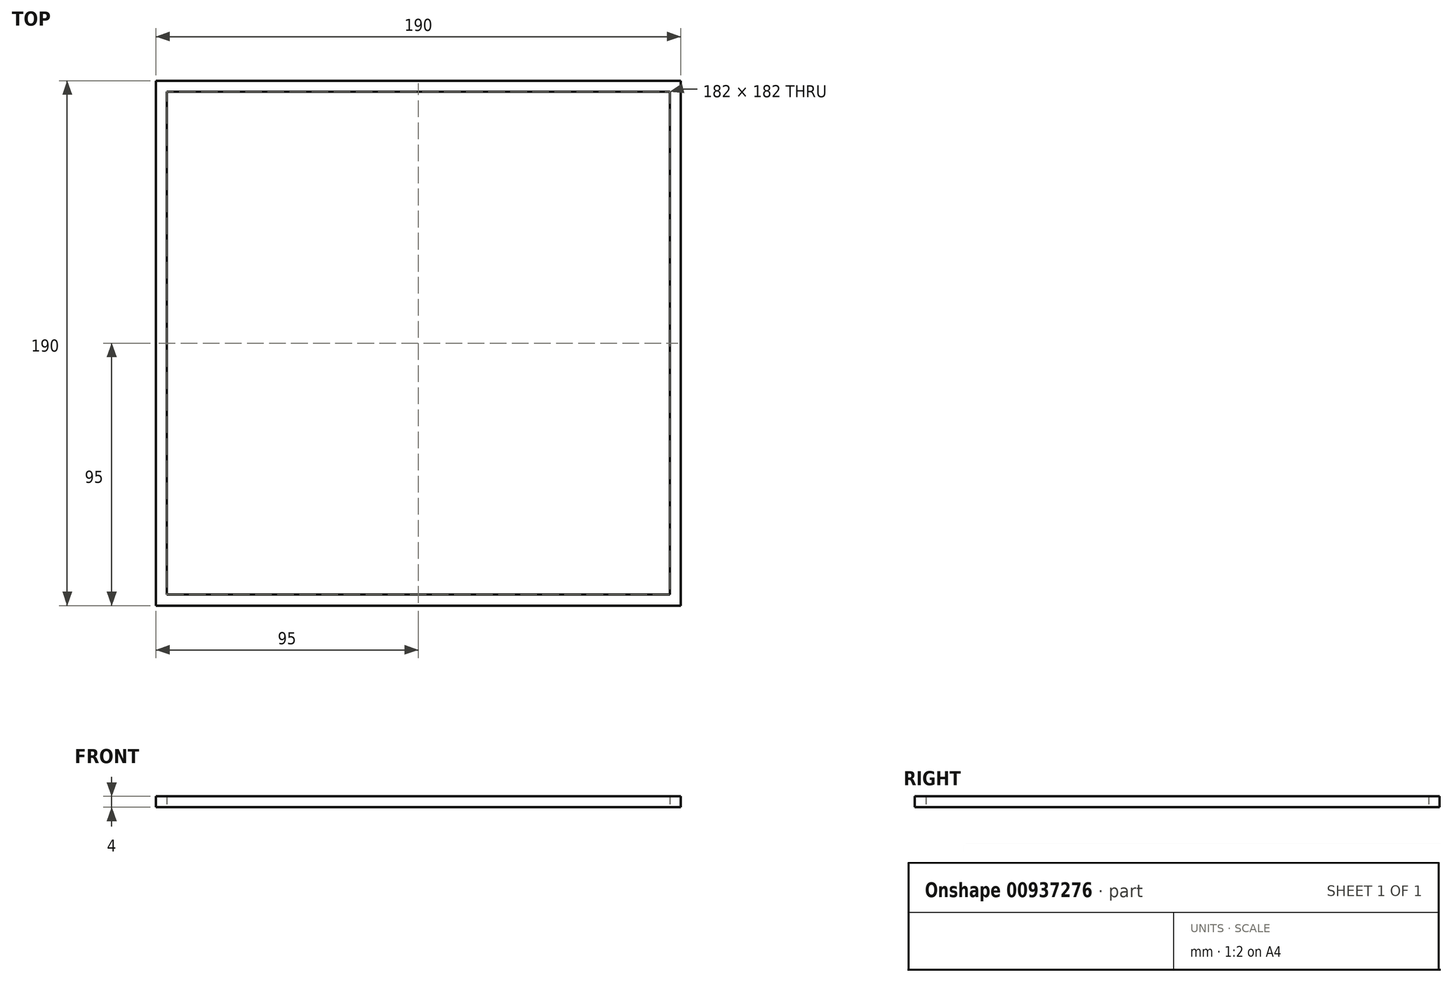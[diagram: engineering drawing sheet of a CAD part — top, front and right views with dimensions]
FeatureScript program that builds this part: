
annotation { "Feature Type Name" : "Feature", "Feature Type Description" : "" }
export const myFeature = defineFeature(function(context is Context, id is Id, definition is map)
    precondition{}
    {
        {
            var Q0;
            Q0=qCreatedBy(makeId("Top.planeOp"),FACE);
            var sketch = newSketch(context, id + "F0", { "sketchPlane" : qUnion([Q0])});
            skLineSegment(sketch, "E0.bottom", {"start": v(-95, 95) * mm, "end": v(95, 95) * mm});
            skLineSegment(sketch, "E0.top", {"start": v(-95, -95) * mm, "end": v(95, -95) * mm});
            skLineSegment(sketch, "E0.left", {"start": v(-95, 95) * mm, "end": v(-95, -95) * mm});
            skLineSegment(sketch, "E0.right", {"start": v(95, 95) * mm, "end": v(95, -95) * mm});
            skPoint(sketch, "E0.middle", {"position": v(0, 0) * mm});
            skLineSegment(sketch, "E1.bottom", {"start": v(-91, 91) * mm, "end": v(91, 91) * mm});
            skLineSegment(sketch, "E1.top", {"start": v(-91, -91) * mm, "end": v(91, -91) * mm});
            skLineSegment(sketch, "E1.left", {"start": v(-91, 91) * mm, "end": v(-91, -91) * mm});
            skLineSegment(sketch, "E1.right", {"start": v(91, 91) * mm, "end": v(91, -91) * mm});
            skSolve(sketch);
        }
        {
            var Q0;
            Q0 = qSketchRegion(id + "F0", true);
            extrude(context, id + "F1", {"entities" : qUnion([Q0]), "depth" : 4 * mm, "offsetDistance" : 25 * mm});
        }
    });
